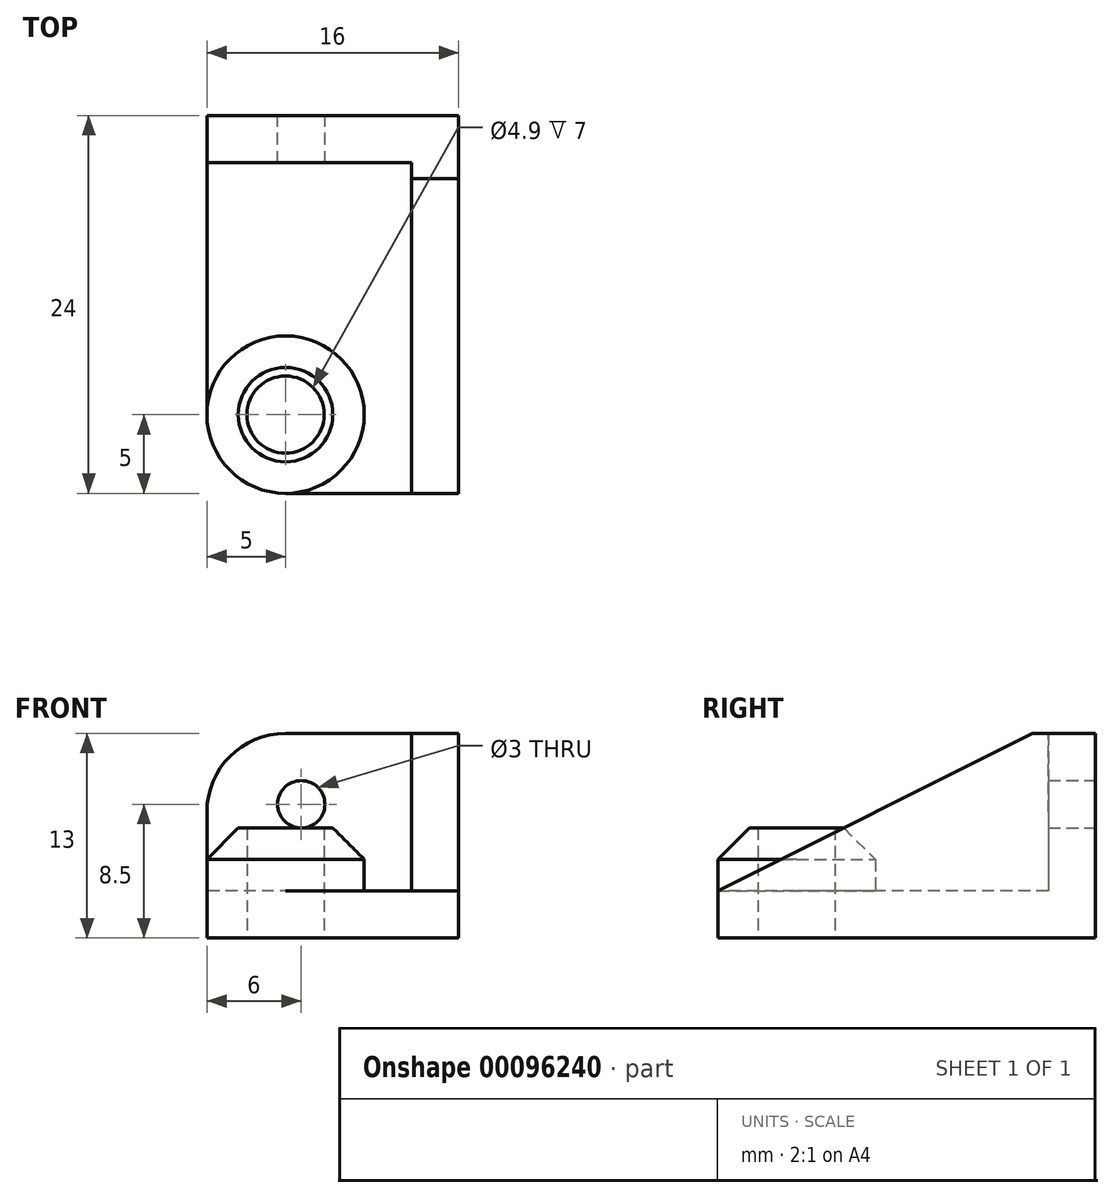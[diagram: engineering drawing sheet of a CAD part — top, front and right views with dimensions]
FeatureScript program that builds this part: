
annotation { "Feature Type Name" : "Feature", "Feature Type Description" : "" }
export const myFeature = defineFeature(function(context is Context, id is Id, definition is map)
    precondition{}
    {
        {
            var Q0;
            Q0=qCreatedBy(makeId("Top.planeOp"),FACE);
            var sketch = newSketch(context, id + "F0", { "sketchPlane" : qUnion([Q0])});
            skLineSegment(sketch, "E0.bottom", {"start": v(0, 24) * mm, "end": v(16, 24) * mm});
            skLineSegment(sketch, "E0.top", {"start": v(0, 0) * mm, "end": v(16, 0) * mm});
            skLineSegment(sketch, "E0.left", {"start": v(0, 24) * mm, "end": v(0, 0) * mm});
            skLineSegment(sketch, "E0.right", {"start": v(16, 24) * mm, "end": v(16, 0) * mm});
            skPoint(sketch, "E1", {"position": v(5, 5) * mm});
            skSolve(sketch);
        }
        {
            var Q0;
            Q0 = qSketchRegion(id + "F0", true);
            extrude(context, id + "F1", {"entities" : qUnion([Q0]), "depth" : 13 * mm});
        }
        {
            var Q0;
            Q0=makeQuery(id+"F1.opExtrude","SWEPT_FACE",FACE,{"disambiguationData":[OSD([sQuery(id+"F0.wireOp",EDGE,"E0.top")])]});
            var Q1;
            Q1=makeQuery(id+"F1.opExtrude","SWEPT_FACE",FACE,{"disambiguationData":[OSD([sQuery(id+"F0.wireOp",EDGE,"E0.left")])]});
            var Q2;
            Q2=makeQuery(id+"F1.opExtrude","CAP_FACE",FACE,{"disambiguationData":[OSD([sQuery(id+"F0.wireOp",EDGE,"E0.bottom"),sQuery(id+"F0.wireOp",EDGE,"E0.top"),sQuery(id+"F0.wireOp",EDGE,"E0.left"),sQuery(id+"F0.wireOp",EDGE,"E0.right"),sQuery(id+"F0.wireOp",EDGE,"2lVPqcIX-aGeb-EN0K-l9k2-6Ow6Fgr4ZdbH")])],"isStart":false});
            shell(context, id + "F2", {"entities" : qUnion([Q0, Q1, Q2]), "thickness" : 3 * mm});
        }
        {
            var Q0;
            Q0=makeQuery(id+"F2.opShell","OFFSET_FACE",FACE,{"disambiguationData":[OSD([sQuery(id+"F0.wireOp",EDGE,"E0.bottom"),sQuery(id+"F0.wireOp",EDGE,"E0.top"),sQuery(id+"F0.wireOp",EDGE,"E0.left"),sQuery(id+"F0.wireOp",EDGE,"E0.right")])]});
            var sketch = newSketch(context, id + "F3", { "sketchPlane" : qUnion([Q0])});
            skPoint(sketch, "E2.0", {"position": v(5, 5) * mm});
            skCircle(sketch, "E3", {"center": v(5, 5) * mm, "radius": 5 * mm});
            skSolve(sketch);
        }
        {
            var Q0;
            Q0 = qSketchRegion(id + "F3", true);
            extrude(context, id + "F4", {"entities" : qUnion([Q0]), "operationType" : NewBodyOperationType.ADD, "depth" : 4 * mm});
        }
        {
            var Q0;
            Q0=sQuery(id+"F0.wireOp",VERTEX,"E1");
            var Q1;
            Q1=makeQuery(id+"F1.opExtrude","SWEPT_BODY",BODY,{"disambiguationData":[OSD([sQuery(id+"F0.wireOp",EDGE,"E0.bottom"),sQuery(id+"F0.wireOp",EDGE,"E0.top"),sQuery(id+"F0.wireOp",EDGE,"E0.left"),sQuery(id+"F0.wireOp",EDGE,"E0.right")])]});
            hole(context, id + "F5", {"style" : HoleStyle.SIMPLE, "endStyle" : HoleEndStyle.THROUGH, "oppositeDirection" : true, "holeDiameter" : 4.9 * mm, "locations" : qUnion([Q0]), "scope" : qUnion([Q1]), "isTappedThrough" : true});
        }
        {
            var Q0;
            Q0=makeQuery(id+"F1.opExtrude","CAP_EDGE",EDGE,{"disambiguationData":[OSD([sQuery(id+"F0.wireOp",EDGE,"E0.top")])],"isStart":false});
            chamfer(context, id + "F6", {"entities" : qUnion([Q0]), "chamferType" : ChamferType.TWO_OFFSETS, "width1" : 20 * mm, "oppositeDirection" : false, "width2" : 10 * mm});
        }
        {
            var Q0;
            Q0=makeQuery(id+"F1.opExtrude","CAP_EDGE",EDGE,{"disambiguationData":[OSD([sQuery(id+"F0.wireOp",EDGE,"E0.left")])],"isStart":false});
            fillet(context, id + "F7", {"entities" : qUnion([Q0]), "radius" : 5 * mm, "tangentPropagation" : true, "allowEdgeOverflow" : false});
        }
        {
            var Q0;
            Q0=makeQuery(id+"F4.opExtrude","CAP_EDGE",EDGE,{"disambiguationData":[OSD([sQuery(id+"F3.wireOp",EDGE,"E3")])],"isStart":false});
            chamfer(context, id + "F8", {"entities" : qUnion([Q0]), "width" : 2 * mm, "tangentPropagation" : true});
        }
        {
            var Q0;
            Q0=makeQuery(id+"F1.opExtrude","SWEPT_FACE",FACE,{"disambiguationData":[OSD([sQuery(id+"F0.wireOp",EDGE,"E0.bottom")])]});
            var sketch = newSketch(context, id + "F9", { "sketchPlane" : qUnion([Q0])});
            skPoint(sketch, "E4", {"position": v(-6, 8.5) * mm});
            skSolve(sketch);
        }
        {
            var Q0;
            Q0=sQuery(id+"F9.wireOp",VERTEX,"E4");
            var Q1;
            Q1=makeQuery(id+"F1.opExtrude","SWEPT_BODY",BODY,{"disambiguationData":[OSD([sQuery(id+"F0.wireOp",EDGE,"E0.bottom"),sQuery(id+"F0.wireOp",EDGE,"E0.top"),sQuery(id+"F0.wireOp",EDGE,"E0.left"),sQuery(id+"F0.wireOp",EDGE,"E0.right")])]});
            hole(context, id + "F10", {"style" : HoleStyle.SIMPLE, "endStyle" : HoleEndStyle.THROUGH, "holeDiameter" : 3 * mm, "locations" : qUnion([Q0]), "scope" : qUnion([Q1]), "isTappedThrough" : true});
        }
        {
            var Q0;
            Q0=makeQuery(id+"F1.opExtrude","SWEPT_EDGE",EDGE,{"disambiguationData":[OSD([sQuery(id+"F0.wireOp",EDGE,"E0.top"),sQuery(id+"F0.wireOp",EDGE,"E0.left")])]});
            fillet(context, id + "F11", {"entities" : qUnion([Q0]), "radius" : 5 * mm, "tangentPropagation" : true, "allowEdgeOverflow" : false});
        }
    });
